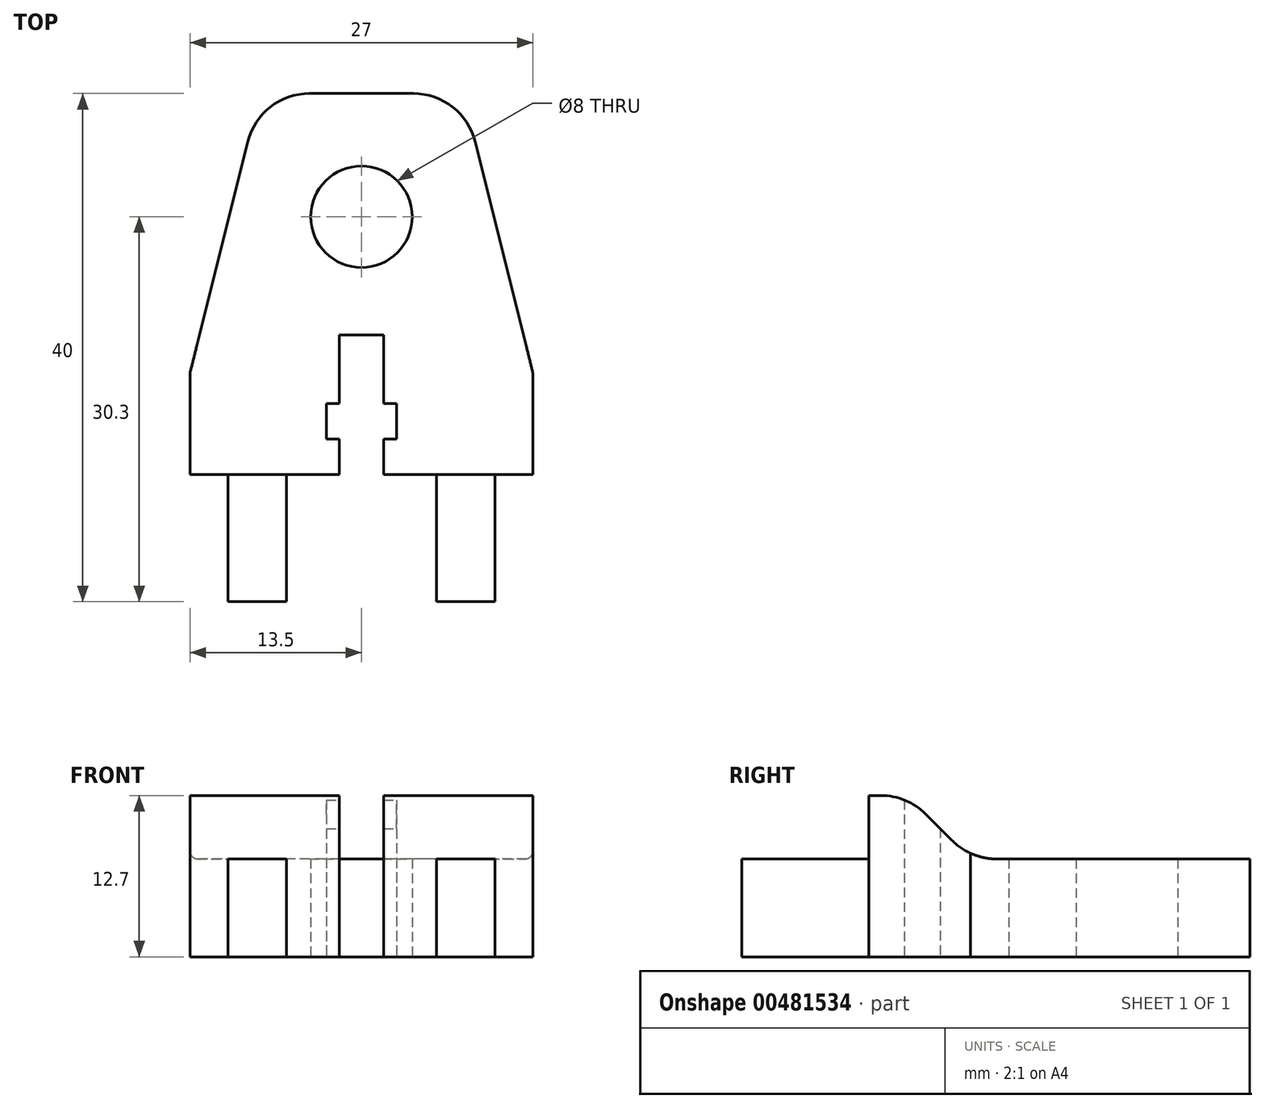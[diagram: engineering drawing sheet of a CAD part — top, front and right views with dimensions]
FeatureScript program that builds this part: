
annotation { "Feature Type Name" : "Feature", "Feature Type Description" : "" }
export const myFeature = defineFeature(function(context is Context, id is Id, definition is map)
    precondition{}
    {
        {
            var Q0;
            Q0=qCreatedBy(makeId("Top.planeOp"),FACE);
            var sketch = newSketch(context, id + "F0", { "sketchPlane" : qUnion([Q0])});
            skLineSegment(sketch, "E0.top", {"start": v(-10.5, 0) * mm, "end": v(-5.9, 0) * mm});
            skLineSegment(sketch, "E1.0.1.0", {"start": v(-13.5, 10) * mm, "end": v(-10.5, 10) * mm});
            skLineSegment(sketch, "E2.bottom", {"start": v(-1.75, 21) * mm, "end": v(1.75, 21) * mm});
            skLineSegment(sketch, "E2.left", {"start": v(-1.75, 21) * mm, "end": v(-1.75, 15.6) * mm});
            skLineSegment(sketch, "E2.right", {"start": v(1.75, 21) * mm, "end": v(1.75, 15.6) * mm});
            skLineSegment(sketch, "E3.bottom", {"start": v(-2.75, 15.6) * mm, "end": v(-1.75, 15.6) * mm});
            skLineSegment(sketch, "E3.top", {"start": v(-2.75, 12.8) * mm, "end": v(-1.75, 12.8) * mm});
            skLineSegment(sketch, "E3.left", {"start": v(-2.75, 15.6) * mm, "end": v(-2.75, 12.8) * mm});
            skLineSegment(sketch, "E3.right", {"start": v(2.75, 15.6) * mm, "end": v(2.75, 12.8) * mm});
            skLineSegment(sketch, "E4.direction2", {"start": v(-1.75, 10) * mm, "end": v(-1.75, 12.8) * mm, "construction": true});
            skLineSegment(sketch, "E5.trimOffspring", {"start": v(1.75, 12.8) * mm, "end": v(2.75, 12.8) * mm});
            skLineSegment(sketch, "E6.trimOffspring", {"start": v(-1.75, 12.8) * mm, "end": v(-1.75, 10) * mm});
            skLineSegment(sketch, "E7.trimOffspring", {"start": v(1.75, 15.6) * mm, "end": v(2.75, 15.6) * mm});
            skLineSegment(sketch, "E8.trimOffspring", {"start": v(1.75, 12.8) * mm, "end": v(1.75, 10) * mm});
            skLineSegment(sketch, "E9.trimOffspring", {"start": v(1.75, 10) * mm, "end": v(5.9, 10) * mm});
            skCircle(sketch, "E10", {"center": v(0, 30.3) * mm, "radius": 4 * mm});
            skLineSegment(sketch, "E11", {"start": v(0, -10.84) * mm, "end": v(0, 49.12) * mm, "construction": true});
            skLineSegment(sketch, "E12.1.0.0", {"start": v(-10.5, 10) * mm, "end": v(-10.5, 0) * mm});
            skLineSegment(sketch, "E13.1.0.0", {"start": v(-5.9, 10) * mm, "end": v(-5.9, 0) * mm});
            skLineSegment(sketch, "E14.trimOffspring", {"start": v(-5.9, 10) * mm, "end": v(-1.75, 10) * mm});
            skLineSegment(sketch, "E15.MirrorCS", {"start": v(10.5, 10) * mm, "end": v(10.5, 0) * mm});
            skLineSegment(sketch, "E16.MirrorCS", {"start": v(10.5, 0) * mm, "end": v(5.9, 0) * mm});
            skLineSegment(sketch, "E17.MirrorCS", {"start": v(5.9, 10) * mm, "end": v(5.9, 0) * mm});
            skLineSegment(sketch, "E18.trimOffspring", {"start": v(10.5, 10) * mm, "end": v(13.5, 10) * mm});
            skLineSegment(sketch, "E19", {"start": v(-13.5, 10) * mm, "end": v(-13.5, 18) * mm});
            skLineSegment(sketch, "E20.MirrorCS", {"start": v(13.5, 10) * mm, "end": v(13.5, 18) * mm});
            skLineSegment(sketch, "E21", {"start": v(-8, 40) * mm, "end": v(8, 40) * mm});
            skLineSegment(sketch, "E22", {"start": v(-13.5, 18) * mm, "end": v(-8, 40) * mm});
            skLineSegment(sketch, "E23", {"start": v(8, 40) * mm, "end": v(13.5, 18) * mm});
            skSolve(sketch);
        }
        {
            var Q0;
            Q0 = qSketchRegion(id + "F0", true);
            extrude(context, id + "F1", {"entities" : qUnion([Q0]), "depth" : 7.7 * mm});
        }
        {
            var Q0;
            Q0=makeQuery(id+"F1.opExtrude","SWEPT_EDGE",EDGE,{"disambiguationData":[OSD([sQuery(id+"F0.wireOp",EDGE,"E21"),sQuery(id+"F0.wireOp",EDGE,"E22")])]});
            var Q1;
            Q1=makeQuery(id+"F1.opExtrude","SWEPT_EDGE",EDGE,{"disambiguationData":[OSD([sQuery(id+"F0.wireOp",EDGE,"E21"),sQuery(id+"F0.wireOp",EDGE,"E23")])]});
            fillet(context, id + "F2", {"entities" : qUnion([Q0, Q1]), "radius" : 5 * mm, "tangentPropagation" : true, "allowEdgeOverflow" : false});
        }
        {
            var Q0;
            Q0=makeQuery(id+"F1.opExtrude","CAP_FACE",FACE,{"disambiguationData":[OSD([sQuery(id+"F0.wireOp",EDGE,"E0.top"),sQuery(id+"F0.wireOp",EDGE,"E1.0.1.0"),sQuery(id+"F0.wireOp",EDGE,"E2.bottom"),sQuery(id+"F0.wireOp",EDGE,"E2.left"),sQuery(id+"F0.wireOp",EDGE,"E2.right"),sQuery(id+"F0.wireOp",EDGE,"E3.bottom"),sQuery(id+"F0.wireOp",EDGE,"E3.top"),sQuery(id+"F0.wireOp",EDGE,"E3.left"),sQuery(id+"F0.wireOp",EDGE,"E3.right"),sQuery(id+"F0.wireOp",EDGE,"E5.trimOffspring"),sQuery(id+"F0.wireOp",EDGE,"E6.trimOffspring"),sQuery(id+"F0.wireOp",EDGE,"E7.trimOffspring"),sQuery(id+"F0.wireOp",EDGE,"E8.trimOffspring"),sQuery(id+"F0.wireOp",EDGE,"E9.trimOffspring"),sQuery(id+"F0.wireOp",EDGE,"E10"),sQuery(id+"F0.wireOp",EDGE,"E12.1.0.0"),sQuery(id+"F0.wireOp",EDGE,"E13.1.0.0"),sQuery(id+"F0.wireOp",EDGE,"E14.trimOffspring"),sQuery(id+"F0.wireOp",EDGE,"E15.MirrorCS"),sQuery(id+"F0.wireOp",EDGE,"E16.MirrorCS"),sQuery(id+"F0.wireOp",EDGE,"E17.MirrorCS"),sQuery(id+"F0.wireOp",EDGE,"E18.trimOffspring"),sQuery(id+"F0.wireOp",EDGE,"E19"),sQuery(id+"F0.wireOp",EDGE,"E20.MirrorCS"),sQuery(id+"F0.wireOp",EDGE,"E21"),sQuery(id+"F0.wireOp",EDGE,"E22"),sQuery(id+"F0.wireOp",EDGE,"E23")])],"isStart":false});
            var sketch = newSketch(context, id + "F3", { "sketchPlane" : qUnion([Q0])});
            skLineSegment(sketch, "E24.left", {"start": v(-1.75, 18) * mm, "end": v(-1.75, 15.6) * mm});
            skLineSegment(sketch, "E24.right", {"start": v(1.75, 18) * mm, "end": v(1.75, 15.6) * mm});
            skLineSegment(sketch, "E25.bottom", {"start": v(-2.75, 15.6) * mm, "end": v(-1.75, 15.6) * mm});
            skLineSegment(sketch, "E25.top", {"start": v(-2.75, 12.8) * mm, "end": v(-1.75, 12.8) * mm});
            skLineSegment(sketch, "E25.left", {"start": v(-2.75, 15.6) * mm, "end": v(-2.75, 12.8) * mm});
            skLineSegment(sketch, "E25.right", {"start": v(2.75, 15.6) * mm, "end": v(2.75, 12.8) * mm});
            skLineSegment(sketch, "E26.direction2", {"start": v(-1.75, 10) * mm, "end": v(-1.75, 12.8) * mm, "construction": true});
            skLineSegment(sketch, "E27.trimOffspring", {"start": v(1.75, 12.8) * mm, "end": v(2.75, 12.8) * mm});
            skLineSegment(sketch, "E28.trimOffspring", {"start": v(-1.75, 12.8) * mm, "end": v(-1.75, 10) * mm});
            skLineSegment(sketch, "E29.trimOffspring", {"start": v(1.75, 15.6) * mm, "end": v(2.75, 15.6) * mm});
            skLineSegment(sketch, "E30.trimOffspring", {"start": v(1.75, 12.8) * mm, "end": v(1.75, 10) * mm});
            skLineSegment(sketch, "E31", {"start": v(-13.5, 10) * mm, "end": v(-13.5, 18) * mm});
            skLineSegment(sketch, "E32.MirrorCS", {"start": v(13.5, 10) * mm, "end": v(13.5, 18) * mm});
            skLineSegment(sketch, "E33", {"start": v(-13.5, 18) * mm, "end": v(-1.75, 18) * mm});
            skLineSegment(sketch, "E34.trimOffspring", {"start": v(1.75, 18) * mm, "end": v(13.5, 18) * mm});
            skLineSegment(sketch, "E35", {"start": v(-13.5, 10) * mm, "end": v(-1.75, 10) * mm});
            skLineSegment(sketch, "E36", {"start": v(1.75, 10) * mm, "end": v(13.5, 10) * mm});
            skSolve(sketch);
        }
        {
            var Q0;
            Q0 = qSketchRegion(id + "F3", true);
            extrude(context, id + "F4", {"entities" : qUnion([Q0]), "operationType" : NewBodyOperationType.ADD, "depth" : 5 * mm});
        }
        {
            var Q0;
            Q0=makeQuery(id+"F4.opExtrude","CAP_EDGE",EDGE,{"disambiguationData":[OSD([sQuery(id+"F3.wireOp",EDGE,"E33")])],"isStart":false});
            var Q1;
            Q1=makeQuery(id+"F4.opExtrude","CAP_EDGE",EDGE,{"disambiguationData":[OSD([sQuery(id+"F3.wireOp",EDGE,"E34.trimOffspring")])],"isStart":false});
            chamfer(context, id + "F5", {"entities" : qUnion([Q0, Q1]), "width" : 5 * mm, "tangentPropagation" : true});
        }
        {
            var Q0;
            {var subQ0=sQuery(id+"F3.wireOp",EDGE,"E33");Q0=makeQuery(id+"F5.opChamfer","BLEND_EDGE",EDGE,{"blendedFrom":[makeQuery(id+"F4.opExtrude","CAP_EDGE",EDGE,{"disambiguationData":[OSD([subQ0])],"isStart":false}),makeQuery(id+"F4.opExtrude","CAP_FACE",FACE,{"disambiguationData":[OSD([sQuery(id+"F3.wireOp",EDGE,"E24.left"),sQuery(id+"F3.wireOp",EDGE,"E25.bottom"),sQuery(id+"F3.wireOp",EDGE,"E25.top"),sQuery(id+"F3.wireOp",EDGE,"E25.left"),sQuery(id+"F3.wireOp",EDGE,"E28.trimOffspring"),sQuery(id+"F3.wireOp",EDGE,"E31"),subQ0,sQuery(id+"F3.wireOp",EDGE,"E35")])],"isStart":false})],"blendedInto":[makeQuery(id+"F4.opExtrude","CAP_FACE",FACE,{"disambiguationData":[OSD([sQuery(id+"F3.wireOp",EDGE,"E24.left"),sQuery(id+"F3.wireOp",EDGE,"E25.bottom"),sQuery(id+"F3.wireOp",EDGE,"E25.top"),sQuery(id+"F3.wireOp",EDGE,"E25.left"),sQuery(id+"F3.wireOp",EDGE,"E28.trimOffspring"),sQuery(id+"F3.wireOp",EDGE,"E31"),subQ0,sQuery(id+"F3.wireOp",EDGE,"E35")])],"isStart":false})]});}
            var Q1;
            {var subQ0=sQuery(id+"F0.wireOp",EDGE,"E20.MirrorCS");var subQ1=sQuery(id+"F0.wireOp",EDGE,"E19");var subQ2=sQuery(id+"F0.wireOp",EDGE,"E22");var subQ3=sQuery(id+"F0.wireOp",EDGE,"E21");var subQ4=sQuery(id+"F0.wireOp",EDGE,"E2.bottom");var subQ5=sQuery(id+"F0.wireOp",EDGE,"E23");var subQ6=sQuery(id+"F0.wireOp",EDGE,"E2.left");var subQ7=sQuery(id+"F0.wireOp",EDGE,"E2.right");var subQ8=sQuery(id+"F3.wireOp",EDGE,"E33");var subQ9=sQuery(id+"F0.wireOp",EDGE,"E10");Q1=makeQuery(id+"F5.opChamfer","BLEND_EDGE",EDGE,{"blendedFrom":[makeQuery(id+"F4.opExtrude","CAP_EDGE",EDGE,{"disambiguationData":[OSD([subQ8])],"isStart":false}),makeQuery(id+"F4.boolean.opBoolean","SPLIT",FACE,{"disambiguationData":[TD([makeQuery(id+"F1.opExtrude","SWEPT_FACE",FACE,{"disambiguationData":[OSD([subQ4])]})])],"derivedFrom":makeQuery(id+"F1.opExtrude","CAP_FACE",FACE,{"disambiguationData":[OSD([sQuery(id+"F0.wireOp",EDGE,"E0.top"),sQuery(id+"F0.wireOp",EDGE,"E1.0.1.0"),subQ4,subQ6,subQ7,sQuery(id+"F0.wireOp",EDGE,"E3.bottom"),sQuery(id+"F0.wireOp",EDGE,"E3.top"),sQuery(id+"F0.wireOp",EDGE,"E3.left"),sQuery(id+"F0.wireOp",EDGE,"E3.right"),sQuery(id+"F0.wireOp",EDGE,"E5.trimOffspring"),sQuery(id+"F0.wireOp",EDGE,"E6.trimOffspring"),sQuery(id+"F0.wireOp",EDGE,"E7.trimOffspring"),sQuery(id+"F0.wireOp",EDGE,"E8.trimOffspring"),sQuery(id+"F0.wireOp",EDGE,"E9.trimOffspring"),subQ9,sQuery(id+"F0.wireOp",EDGE,"E12.1.0.0"),sQuery(id+"F0.wireOp",EDGE,"E13.1.0.0"),sQuery(id+"F0.wireOp",EDGE,"E14.trimOffspring"),sQuery(id+"F0.wireOp",EDGE,"E15.MirrorCS"),sQuery(id+"F0.wireOp",EDGE,"E16.MirrorCS"),sQuery(id+"F0.wireOp",EDGE,"E17.MirrorCS"),sQuery(id+"F0.wireOp",EDGE,"E18.trimOffspring"),subQ1,subQ0,subQ3,subQ2,subQ5])],"isStart":false})})],"blendedInto":[makeQuery(id+"F4.boolean.opBoolean","SPLIT",FACE,{"disambiguationData":[TD([makeQuery(id+"F1.opExtrude","SWEPT_FACE",FACE,{"disambiguationData":[OSD([subQ4])]})])],"derivedFrom":makeQuery(id+"F1.opExtrude","CAP_FACE",FACE,{"disambiguationData":[OSD([sQuery(id+"F0.wireOp",EDGE,"E0.top"),sQuery(id+"F0.wireOp",EDGE,"E1.0.1.0"),subQ4,subQ6,subQ7,sQuery(id+"F0.wireOp",EDGE,"E3.bottom"),sQuery(id+"F0.wireOp",EDGE,"E3.top"),sQuery(id+"F0.wireOp",EDGE,"E3.left"),sQuery(id+"F0.wireOp",EDGE,"E3.right"),sQuery(id+"F0.wireOp",EDGE,"E5.trimOffspring"),sQuery(id+"F0.wireOp",EDGE,"E6.trimOffspring"),sQuery(id+"F0.wireOp",EDGE,"E7.trimOffspring"),sQuery(id+"F0.wireOp",EDGE,"E8.trimOffspring"),sQuery(id+"F0.wireOp",EDGE,"E9.trimOffspring"),subQ9,sQuery(id+"F0.wireOp",EDGE,"E12.1.0.0"),sQuery(id+"F0.wireOp",EDGE,"E13.1.0.0"),sQuery(id+"F0.wireOp",EDGE,"E14.trimOffspring"),sQuery(id+"F0.wireOp",EDGE,"E15.MirrorCS"),sQuery(id+"F0.wireOp",EDGE,"E16.MirrorCS"),sQuery(id+"F0.wireOp",EDGE,"E17.MirrorCS"),sQuery(id+"F0.wireOp",EDGE,"E18.trimOffspring"),subQ1,subQ0,subQ3,subQ2,subQ5])],"isStart":false})})]});}
            var Q2;
            {var subQ0=sQuery(id+"F3.wireOp",EDGE,"E34.trimOffspring");Q2=makeQuery(id+"F5.opChamfer","BLEND_EDGE",EDGE,{"blendedFrom":[makeQuery(id+"F4.opExtrude","CAP_EDGE",EDGE,{"disambiguationData":[OSD([subQ0])],"isStart":false}),makeQuery(id+"F4.opExtrude","CAP_FACE",FACE,{"disambiguationData":[OSD([sQuery(id+"F3.wireOp",EDGE,"E24.right"),sQuery(id+"F3.wireOp",EDGE,"E25.right"),sQuery(id+"F3.wireOp",EDGE,"E27.trimOffspring"),sQuery(id+"F3.wireOp",EDGE,"E29.trimOffspring"),sQuery(id+"F3.wireOp",EDGE,"E30.trimOffspring"),sQuery(id+"F3.wireOp",EDGE,"E32.MirrorCS"),subQ0,sQuery(id+"F3.wireOp",EDGE,"E36")])],"isStart":false})],"blendedInto":[makeQuery(id+"F4.opExtrude","CAP_FACE",FACE,{"disambiguationData":[OSD([sQuery(id+"F3.wireOp",EDGE,"E24.right"),sQuery(id+"F3.wireOp",EDGE,"E25.right"),sQuery(id+"F3.wireOp",EDGE,"E27.trimOffspring"),sQuery(id+"F3.wireOp",EDGE,"E29.trimOffspring"),sQuery(id+"F3.wireOp",EDGE,"E30.trimOffspring"),sQuery(id+"F3.wireOp",EDGE,"E32.MirrorCS"),subQ0,sQuery(id+"F3.wireOp",EDGE,"E36")])],"isStart":false})]});}
            var Q3;
            {var subQ0=sQuery(id+"F0.wireOp",EDGE,"E20.MirrorCS");var subQ1=sQuery(id+"F0.wireOp",EDGE,"E19");var subQ2=sQuery(id+"F0.wireOp",EDGE,"E22");var subQ3=sQuery(id+"F0.wireOp",EDGE,"E21");var subQ4=sQuery(id+"F0.wireOp",EDGE,"E2.bottom");var subQ5=sQuery(id+"F0.wireOp",EDGE,"E23");var subQ6=sQuery(id+"F0.wireOp",EDGE,"E2.left");var subQ7=sQuery(id+"F0.wireOp",EDGE,"E2.right");var subQ8=sQuery(id+"F0.wireOp",EDGE,"E10");var subQ9=sQuery(id+"F3.wireOp",EDGE,"E34.trimOffspring");Q3=makeQuery(id+"F5.opChamfer","BLEND_EDGE",EDGE,{"blendedFrom":[makeQuery(id+"F4.opExtrude","CAP_EDGE",EDGE,{"disambiguationData":[OSD([subQ9])],"isStart":false}),makeQuery(id+"F4.boolean.opBoolean","SPLIT",FACE,{"disambiguationData":[TD([makeQuery(id+"F1.opExtrude","SWEPT_FACE",FACE,{"disambiguationData":[OSD([subQ4])]})])],"derivedFrom":makeQuery(id+"F1.opExtrude","CAP_FACE",FACE,{"disambiguationData":[OSD([sQuery(id+"F0.wireOp",EDGE,"E0.top"),sQuery(id+"F0.wireOp",EDGE,"E1.0.1.0"),subQ4,subQ6,subQ7,sQuery(id+"F0.wireOp",EDGE,"E3.bottom"),sQuery(id+"F0.wireOp",EDGE,"E3.top"),sQuery(id+"F0.wireOp",EDGE,"E3.left"),sQuery(id+"F0.wireOp",EDGE,"E3.right"),sQuery(id+"F0.wireOp",EDGE,"E5.trimOffspring"),sQuery(id+"F0.wireOp",EDGE,"E6.trimOffspring"),sQuery(id+"F0.wireOp",EDGE,"E7.trimOffspring"),sQuery(id+"F0.wireOp",EDGE,"E8.trimOffspring"),sQuery(id+"F0.wireOp",EDGE,"E9.trimOffspring"),subQ8,sQuery(id+"F0.wireOp",EDGE,"E12.1.0.0"),sQuery(id+"F0.wireOp",EDGE,"E13.1.0.0"),sQuery(id+"F0.wireOp",EDGE,"E14.trimOffspring"),sQuery(id+"F0.wireOp",EDGE,"E15.MirrorCS"),sQuery(id+"F0.wireOp",EDGE,"E16.MirrorCS"),sQuery(id+"F0.wireOp",EDGE,"E17.MirrorCS"),sQuery(id+"F0.wireOp",EDGE,"E18.trimOffspring"),subQ1,subQ0,subQ3,subQ2,subQ5])],"isStart":false})})],"blendedInto":[makeQuery(id+"F4.boolean.opBoolean","SPLIT",FACE,{"disambiguationData":[TD([makeQuery(id+"F1.opExtrude","SWEPT_FACE",FACE,{"disambiguationData":[OSD([subQ4])]})])],"derivedFrom":makeQuery(id+"F1.opExtrude","CAP_FACE",FACE,{"disambiguationData":[OSD([sQuery(id+"F0.wireOp",EDGE,"E0.top"),sQuery(id+"F0.wireOp",EDGE,"E1.0.1.0"),subQ4,subQ6,subQ7,sQuery(id+"F0.wireOp",EDGE,"E3.bottom"),sQuery(id+"F0.wireOp",EDGE,"E3.top"),sQuery(id+"F0.wireOp",EDGE,"E3.left"),sQuery(id+"F0.wireOp",EDGE,"E3.right"),sQuery(id+"F0.wireOp",EDGE,"E5.trimOffspring"),sQuery(id+"F0.wireOp",EDGE,"E6.trimOffspring"),sQuery(id+"F0.wireOp",EDGE,"E7.trimOffspring"),sQuery(id+"F0.wireOp",EDGE,"E8.trimOffspring"),sQuery(id+"F0.wireOp",EDGE,"E9.trimOffspring"),subQ8,sQuery(id+"F0.wireOp",EDGE,"E12.1.0.0"),sQuery(id+"F0.wireOp",EDGE,"E13.1.0.0"),sQuery(id+"F0.wireOp",EDGE,"E14.trimOffspring"),sQuery(id+"F0.wireOp",EDGE,"E15.MirrorCS"),sQuery(id+"F0.wireOp",EDGE,"E16.MirrorCS"),sQuery(id+"F0.wireOp",EDGE,"E17.MirrorCS"),sQuery(id+"F0.wireOp",EDGE,"E18.trimOffspring"),subQ1,subQ0,subQ3,subQ2,subQ5])],"isStart":false})})]});}
            fillet(context, id + "F6", {"entities" : qUnion([Q0, Q1, Q2, Q3]), "radius" : 5 * mm, "tangentPropagation" : true, "allowEdgeOverflow" : false});
        }
    });
